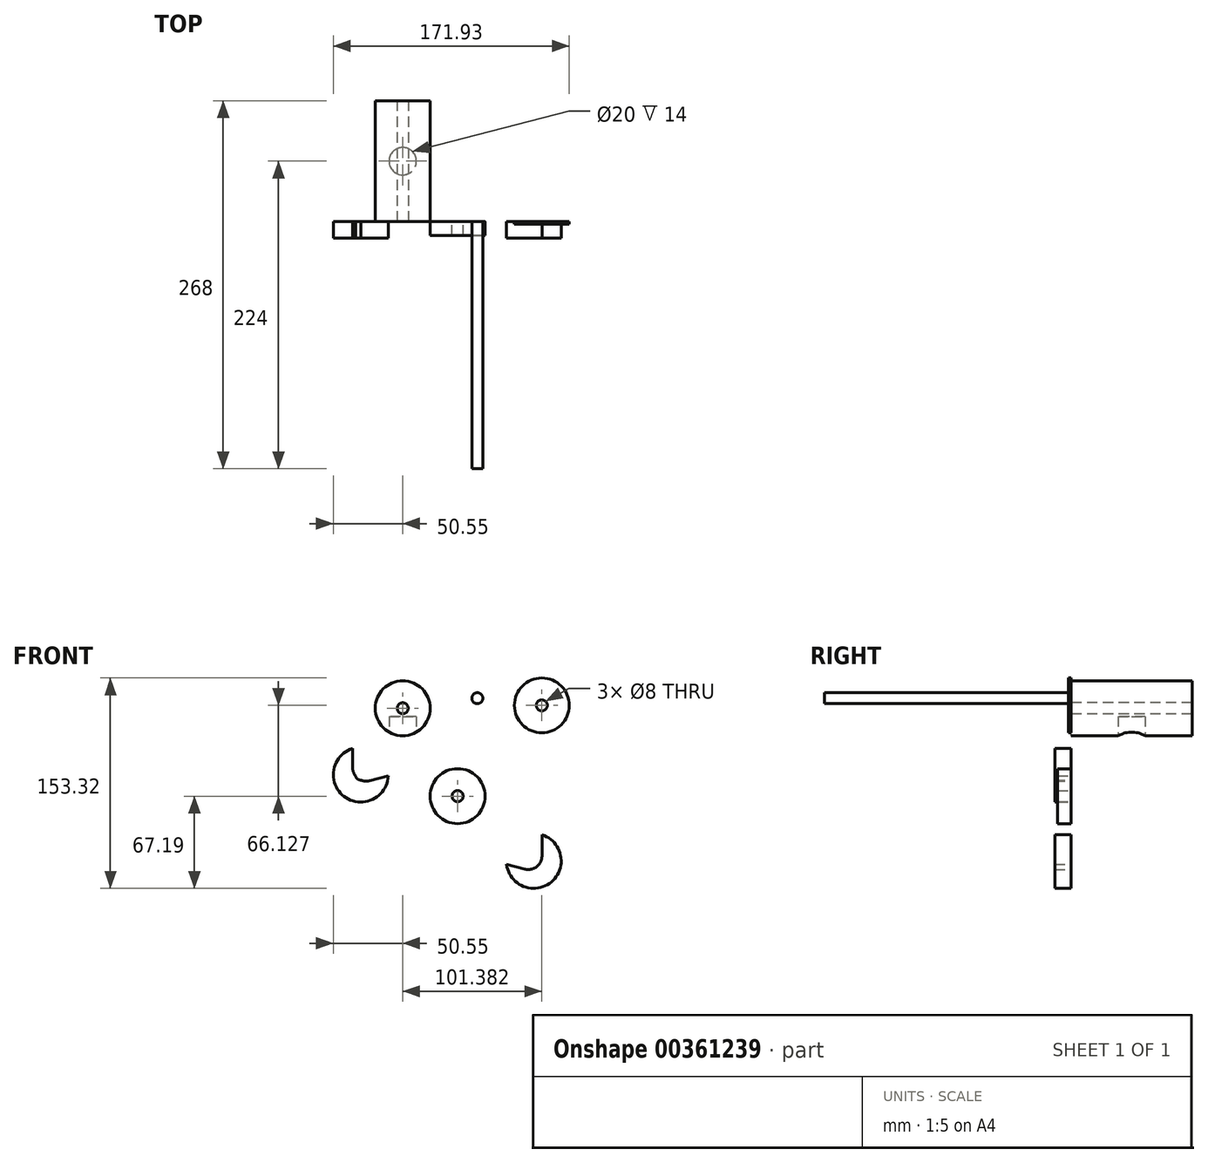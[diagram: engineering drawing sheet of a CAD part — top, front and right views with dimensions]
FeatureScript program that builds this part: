
annotation { "Feature Type Name" : "Feature", "Feature Type Description" : "" }
export const myFeature = defineFeature(function(context is Context, id is Id, definition is map)
    precondition{}
    {
        {
            var Q0;
            Q0=qCreatedBy(makeId("Front.planeOp"),FACE);
            var sketch = newSketch(context, id + "F0", { "sketchPlane" : qUnion([Q0])});
            skCircle(sketch, "E0", {"center": v(0, 0) * mm, "radius": 20 * mm});
            skCircle(sketch, "E1", {"center": v(0, 0) * mm, "radius": 4 * mm});
            skSolve(sketch);
        }
        {
            var Q0;
            Q0 = qSketchRegion(id + "F0", true);
            extrude(context, id + "F1", {"entities" : qUnion([Q0]), "depth" : 10 * mm});
        }
        {
            var Q0;
            Q0=qCreatedBy(makeId("Front.planeOp"),FACE);
            var sketch = newSketch(context, id + "F2", { "sketchPlane" : qUnion([Q0])});
            skArc(sketch, "E2", {"start": v(-76.55, 34.74) * mm, "mid": v(-82.72, -0.2) * mm, "end": v(-50.57, 14.8) * mm});
            skCircle(sketch, "E3", {"center": v(-70.55, 15.66) * mm, "radius": 4 * mm});
            skLineSegment(sketch, "E4", {"start": v(-76.55, 34.74) * mm, "end": v(-76.55, 20.87) * mm});
            skLineSegment(sketch, "E5", {"start": v(-63.96, 11.21) * mm, "end": v(-50.57, 14.8) * mm});
            skPoint(sketch, "E6.visualSharp", {"position": v(-76.55, 7.84) * mm});
            skArc(sketch, "E6.filletArc", {"start": v(-76.55, 20.87) * mm, "mid": v(-72.64, 12.94) * mm, "end": v(-63.96, 11.21) * mm});
            skSolve(sketch);
        }
        {
            var Q0;
            Q0=makeQuery(id+"F2.imprint","IMPRINT",FACE,{"disambiguationData":[TD([[makeQuery(id+"F2.imprint","IMPRINT",EDGE,{"derivedFrom":sQuery(id+"F2.wireOp",EDGE,"E2")}),1.0]])]});
            extrude(context, id + "F3", {"entities" : qUnion([Q0]), "depth" : 12 * mm});
        }
        {
            var Q0;
            Q0=qCreatedBy(makeId("Front.planeOp"),FACE);
            var sketch = newSketch(context, id + "F4", { "sketchPlane" : qUnion([Q0])});
            skCircle(sketch, "E7", {"center": v(61.38, 66.13) * mm, "radius": 20 * mm});
            skCircle(sketch, "E8", {"center": v(61.38, 66.13) * mm, "radius": 4 * mm});
            skSolve(sketch);
        }
        {
            var Q0;
            Q0 = qSketchRegion(id + "F4", true);
            extrude(context, id + "F5", {"entities" : qUnion([Q0]), "depth" : 2 * mm});
        }
        {
            var Q0;
            Q0=qCreatedBy(makeId("Front.planeOp"),FACE);
            var sketch = newSketch(context, id + "F6", { "sketchPlane" : qUnion([Q0])});
            skCircle(sketch, "E9", {"center": v(-40, 64) * mm, "radius": 20 * mm});
            skCircle(sketch, "E10", {"center": v(-40, 64) * mm, "radius": 4 * mm});
            skSolve(sketch);
        }
        {
            var Q0;
            Q0 = qSketchRegion(id + "F6", true);
            extrude(context, id + "F7", {"entities" : qUnion([Q0]), "oppositeDirection" : true, "depth" : 88 * mm});
        }
        {
            var Q0;
            Q0=qCreatedBy(makeId("Front.planeOp"),FACE);
            var sketch = newSketch(context, id + "F8", { "sketchPlane" : qUnion([Q0])});
            skArc(sketch, "E11", {"start": v(35.6, -49.63) * mm, "mid": v(68.25, -62.56) * mm, "end": v(61.45, -28.1) * mm});
            skCircle(sketch, "E12", {"center": v(55.45, -47.19) * mm, "radius": 4 * mm});
            skLineSegment(sketch, "E13", {"start": v(61.45, -28.1) * mm, "end": v(61.45, -43.53) * mm});
            skLineSegment(sketch, "E14", {"start": v(48.86, -53.19) * mm, "end": v(35.6, -49.63) * mm});
            skPoint(sketch, "E15.visualSharp", {"position": v(61.45, -56.56) * mm});
            skArc(sketch, "E15.filletArc", {"start": v(48.86, -53.19) * mm, "mid": v(57.54, -51.46) * mm, "end": v(61.45, -43.53) * mm});
            skSolve(sketch);
        }
        {
            var Q0;
            Q0=makeQuery(id+"F8.imprint","IMPRINT",FACE,{"disambiguationData":[TD([[makeQuery(id+"F8.imprint","IMPRINT",EDGE,{"derivedFrom":sQuery(id+"F8.wireOp",EDGE,"E11")}),1.0]])]});
            extrude(context, id + "F9", {"entities" : qUnion([Q0]), "depth" : 12 * mm});
        }
        {
            var Q0;
            Q0=qCreatedBy(makeId("Front.planeOp"),FACE);
            var sketch = newSketch(context, id + "F10", { "sketchPlane" : qUnion([Q0])});
            skCircle(sketch, "E16", {"center": v(14.41, 71.33) * mm, "radius": 4 * mm});
            skSolve(sketch);
        }
        {
            var Q0;
            Q0 = qSketchRegion(id + "F10", true);
            extrude(context, id + "F11", {"entities" : qUnion([Q0]), "depth" : 180 * mm});
        }
        {
            var Q0;
            Q0=qCreatedBy(makeId("Top.planeOp"),FACE);
            var sketch = newSketch(context, id + "F12", { "sketchPlane" : qUnion([Q0])});
            skCircle(sketch, "E17", {"center": v(-40, 44) * mm, "radius": 10 * mm});
            skSolve(sketch);
        }
        {
            var Q0;
            Q0 = qSketchRegion(id + "F12", true);
            extrude(context, id + "F13", {"entities" : qUnion([Q0]), "operationType" : NewBodyOperationType.REMOVE, "depth" : 58 * mm});
        }
    });
